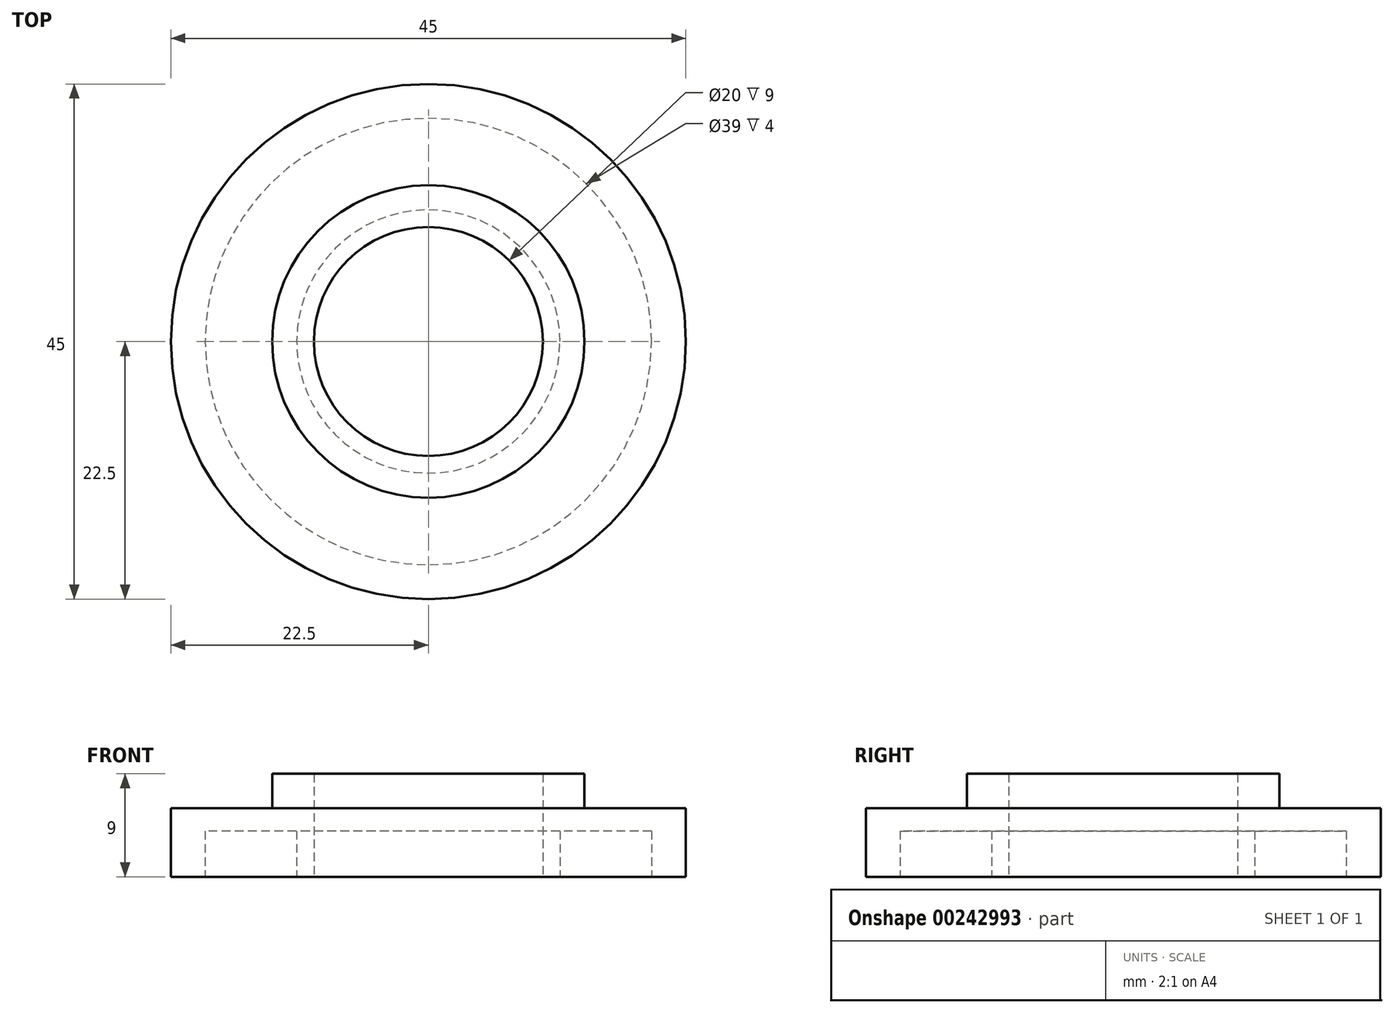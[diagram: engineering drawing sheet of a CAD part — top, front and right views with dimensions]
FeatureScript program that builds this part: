
annotation { "Feature Type Name" : "Feature", "Feature Type Description" : "" }
export const myFeature = defineFeature(function(context is Context, id is Id, definition is map)
    precondition{}
    {
        {
            var Q0;
            Q0=qCreatedBy(makeId("Top.planeOp"),FACE);
            var sketch = newSketch(context, id + "F0", { "sketchPlane" : qUnion([Q0])});
            skCircle(sketch, "E0", {"center": v(0, 0) * mm, "radius": 22.5 * mm});
            skCircle(sketch, "E1", {"center": v(0, 0) * mm, "radius": 15.5 * mm, "construction": true});
            skCircle(sketch, "E2", {"center": v(0, 0) * mm, "radius": 10 * mm});
            skCircle(sketch, "E3", {"center": v(15.5, 0) * mm, "radius": 3.25 * mm, "construction": true});
            skCircle(sketch, "E4", {"center": v(-7.75, 13.42) * mm, "radius": 3.25 * mm, "construction": true});
            skCircle(sketch, "E5", {"center": v(-7.75, -13.42) * mm, "radius": 3.25 * mm, "construction": true});
            skLineSegment(sketch, "E6", {"start": v(-7.75, -13.42) * mm, "end": v(0, 0) * mm, "construction": true});
            skLineSegment(sketch, "E7", {"start": v(-7.75, 13.42) * mm, "end": v(0, 0) * mm, "construction": true});
            skSolve(sketch);
        }
        {
            var Q0;
            Q0 = qSketchRegion(id + "F0", true);
            extrude(context, id + "F1", {"entities" : qUnion([Q0]), "depth" : 6 * mm});
        }
        {
            var Q0;
            Q0=makeQuery(id+"F1.opExtrude","CAP_FACE",FACE,{"disambiguationData":[OSD([sQuery(id+"F0.wireOp",EDGE,"E0"),sQuery(id+"F0.wireOp",EDGE,"E2")])],"isStart":false});
            var sketch = newSketch(context, id + "F2", { "sketchPlane" : qUnion([Q0])});
            skCircle(sketch, "E8", {"center": v(0, 0) * mm, "radius": 13.65 * mm});
            skCircle(sketch, "E9", {"center": v(0, 0) * mm, "radius": 10 * mm});
            skSolve(sketch);
        }
        {
            var Q0;
            Q0 = qSketchRegion(id + "F2", true);
            extrude(context, id + "F3", {"entities" : qUnion([Q0]), "operationType" : NewBodyOperationType.ADD, "depth" : 3 * mm});
        }
        {
            var Q0;
            Q0=makeQuery(id+"F0.imprint","IMPRINT",FACE,{"disambiguationData":[TD([[makeQuery(id+"F0.imprint","IMPRINT",EDGE,{"derivedFrom":sQuery(id+"F0.wireOp",EDGE,"E0")}),1.0]])]});
            var sketch = newSketch(context, id + "F4", { "sketchPlane" : qUnion([Q0])});
            skCircle(sketch, "E10", {"center": v(0, 0) * mm, "radius": 11.5 * mm});
            skCircle(sketch, "E11", {"center": v(0, 0) * mm, "radius": 19.5 * mm});
            skSolve(sketch);
        }
        {
            var Q0;
            Q0 = qSketchRegion(id + "F4", true);
            extrude(context, id + "F5", {"entities" : qUnion([Q0]), "operationType" : NewBodyOperationType.REMOVE, "depth" : 4 * mm});
        }
    });
